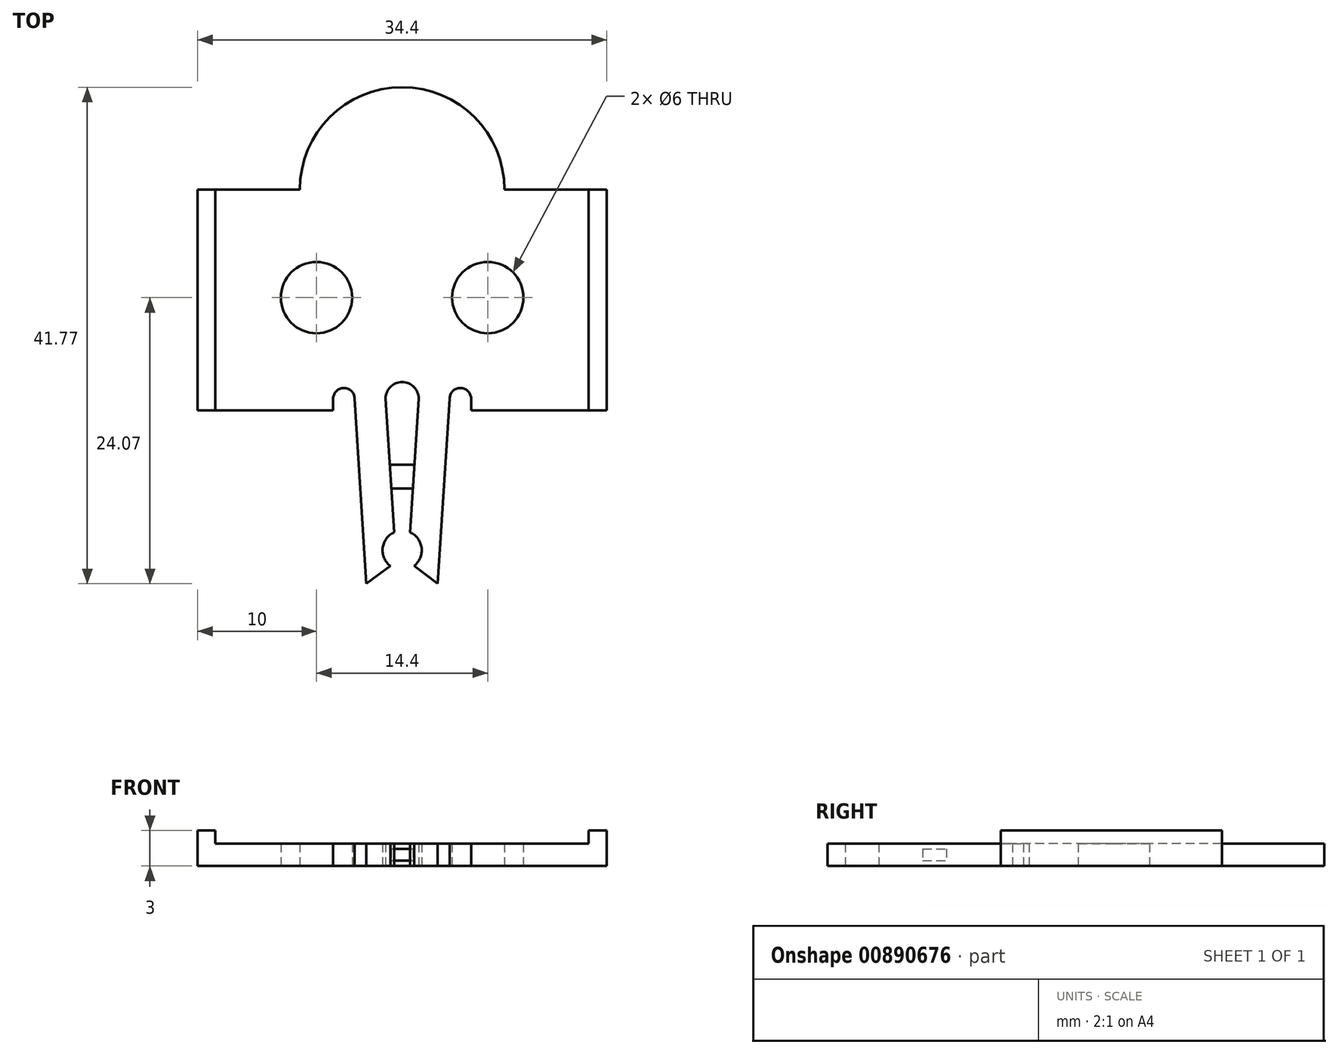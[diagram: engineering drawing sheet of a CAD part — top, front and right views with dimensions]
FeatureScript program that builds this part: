
annotation { "Feature Type Name" : "Feature", "Feature Type Description" : "" }
export const myFeature = defineFeature(function(context is Context, id is Id, definition is map)
    precondition{}
    {
        {
            var Q0;
            Q0=qCreatedBy(makeId("Top.planeOp"),FACE);
            var sketch = newSketch(context, id + "F0", { "sketchPlane" : qUnion([Q0])});
            skLineSegment(sketch, "E0", {"start": v(-5.8, 0) * mm, "end": v(-17.2, 0) * mm});
            skLineSegment(sketch, "E1", {"start": v(-17.2, 0) * mm, "end": v(-17.2, 18.6) * mm});
            skLineSegment(sketch, "E2", {"start": v(-17.2, 18.6) * mm, "end": v(0, 18.6) * mm});
            skLineSegment(sketch, "E3", {"start": v(-5.8, 0) * mm, "end": v(-5.8, 1) * mm});
            skLineSegment(sketch, "E4", {"start": v(-4, 1) * mm, "end": v(-3, -14.57) * mm});
            skLineSegment(sketch, "E5", {"start": v(-3, -14.57) * mm, "end": v(-1, -13.07) * mm});
            skLineSegment(sketch, "E6", {"start": v(-0.67, -10.25) * mm, "end": v(-0.67, -10.25) * mm});
            skLineSegment(sketch, "E7", {"start": v(-0.67, -10.25) * mm, "end": v(-1.4, 1) * mm});
            skArc(sketch, "E8", {"start": v(-1, -13.07) * mm, "mid": v(1.64, -11.95) * mm, "end": v(-0.67, -10.25) * mm, "construction": true});
            skArc(sketch, "E9", {"start": v(-0.67, -10.25) * mm, "mid": v(-1.64, -11.56) * mm, "end": v(-1, -13.07) * mm});
            skArc(sketch, "E10", {"start": v(-5.8, 1) * mm, "mid": v(-4.9, 0.1) * mm, "end": v(-4, 1) * mm, "construction": true});
            skArc(sketch, "E11", {"start": v(-4, 1) * mm, "mid": v(-4.9, 1.9) * mm, "end": v(-5.8, 1) * mm});
            skLineSegment(sketch, "E12", {"start": v(0, 0) * mm, "end": v(0, 3.93) * mm, "construction": true});
            skArc(sketch, "E13", {"start": v(-1.4, 1) * mm, "mid": v(0.99, 0.01) * mm, "end": v(0, 2.4) * mm, "construction": true});
            skArc(sketch, "E14", {"start": v(0, 2.4) * mm, "mid": v(-0.99, 1.99) * mm, "end": v(-1.4, 1) * mm});
            skArc(sketch, "E15.MirrorCS", {"start": v(1.4, 1) * mm, "mid": v(-0.99, 0.01) * mm, "end": v(0, 2.4) * mm, "construction": true});
            skCircle(sketch, "E16", {"center": v(-7.2, 9.5) * mm, "radius": 3 * mm});
            skLineSegment(sketch, "E17.MirrorCS", {"start": v(5.8, 0) * mm, "end": v(5.8, 1) * mm});
            skArc(sketch, "E18.MirrorCS", {"start": v(5.8, 1) * mm, "mid": v(4.9, 0.1) * mm, "end": v(4, 1) * mm, "construction": true});
            skArc(sketch, "E19.MirrorCS", {"start": v(0, 2.4) * mm, "mid": v(0.99, 1.99) * mm, "end": v(1.4, 1) * mm});
            skArc(sketch, "E20.MirrorCS", {"start": v(4, 1) * mm, "mid": v(4.9, 1.9) * mm, "end": v(5.8, 1) * mm});
            skArc(sketch, "E21.MirrorCS", {"start": v(0.67, -10.25) * mm, "mid": v(1.64, -11.56) * mm, "end": v(1, -13.07) * mm});
            skLineSegment(sketch, "E22.MirrorCS", {"start": v(3, -14.57) * mm, "end": v(1, -13.07) * mm});
            skArc(sketch, "E23.MirrorCS", {"start": v(1, -13.07) * mm, "mid": v(-1.64, -11.95) * mm, "end": v(0.67, -10.25) * mm, "construction": true});
            skLineSegment(sketch, "E24.MirrorCS", {"start": v(0.67, -10.25) * mm, "end": v(1.4, 1) * mm});
            skLineSegment(sketch, "E25.MirrorCS", {"start": v(4, 1) * mm, "end": v(3, -14.57) * mm});
            skCircle(sketch, "E26.MirrorC", {"center": v(7.2, 9.5) * mm, "radius": 3 * mm});
            skLineSegment(sketch, "E27.MirrorCS", {"start": v(5.8, 0) * mm, "end": v(17.2, 0) * mm});
            skLineSegment(sketch, "E28.MirrorCS", {"start": v(17.2, 18.6) * mm, "end": v(0, 18.6) * mm});
            skLineSegment(sketch, "E29.MirrorCS", {"start": v(17.2, 0) * mm, "end": v(17.2, 18.6) * mm});
            skLineSegment(sketch, "E30.MirrorCS", {"start": v(0.67, -10.25) * mm, "end": v(0.67, -10.25) * mm});
            skLineSegment(sketch, "E31", {"start": v(1.04, -4.57) * mm, "end": v(-1.04, -4.57) * mm});
            skLineSegment(sketch, "E32", {"start": v(-0.9, -6.57) * mm, "end": v(0.9, -6.57) * mm});
            skLineSegment(sketch, "E33", {"start": v(-15.7, 18.6) * mm, "end": v(-15.7, 0) * mm});
            skLineSegment(sketch, "E34", {"start": v(15.7, 18.6) * mm, "end": v(15.7, 0) * mm});
            skCircle(sketch, "E35", {"center": v(0, 18.6) * mm, "radius": 8.6 * mm});
            skSolve(sketch);
        }
        {
            var Q0;
            {var subQ11=sQuery(id+"F0.wireOp",EDGE,"E3");Q0=makeQuery(id+"F0.imprint","IMPRINT",FACE,{"disambiguationData":[TD([[makeQuery(id+"F0.imprint","IMPRINT",EDGE,{"derivedFrom":subQ11}),1.0]])]});}
            var Q1;
            {var subQ3=sQuery(id+"F0.wireOp",EDGE,"E28.MirrorCS");var subQ4=sQuery(id+"F0.wireOp",EDGE,"E2");var subQ5=makeQuery(id+"F0.imprint","INTERSECT",VERTEX,{"derivedFrom":[subQ4,subQ3]});Q1=makeQuery(id+"F0.imprint","IMPRINT",FACE,{"disambiguationData":[TD([[makeQuery(id+"F0.imprint","IMPRINT",EDGE,{"disambiguationData":[TD([[subQ5,1.0]])],"derivedFrom":subQ4}),-1.0]])]});}
            var Q2;
            {var subQ0=sQuery(id+"F0.wireOp",EDGE,"E28.MirrorCS");var subQ1=sQuery(id+"F0.wireOp",EDGE,"E2");var subQ2=makeQuery(id+"F0.imprint","INTERSECT",VERTEX,{"derivedFrom":[subQ1,subQ0]});Q2=makeQuery(id+"F0.imprint","IMPRINT",FACE,{"disambiguationData":[TD([[makeQuery(id+"F0.imprint","IMPRINT",EDGE,{"disambiguationData":[TD([[subQ2,1.0]])],"derivedFrom":subQ1}),1.0]])]});}
            extrude(context, id + "F1", {"entities" : qUnion([Q0, Q1, Q2]), "depth" : 1.9 * mm, "offsetDistance" : 25 * mm});
        }
        {
            var Q0;
            {var subQ0=sQuery(id+"F0.wireOp",EDGE,"E1");Q0=makeQuery(id+"F0.imprint","IMPRINT",FACE,{"disambiguationData":[TD([[makeQuery(id+"F0.imprint","IMPRINT",EDGE,{"derivedFrom":subQ0}),-1.0]])]});}
            var Q1;
            {var subQ0=sQuery(id+"F0.wireOp",EDGE,"E29.MirrorCS");Q1=makeQuery(id+"F0.imprint","IMPRINT",FACE,{"disambiguationData":[TD([[makeQuery(id+"F0.imprint","IMPRINT",EDGE,{"derivedFrom":subQ0}),1.0]])]});}
            extrude(context, id + "F2", {"entities" : qUnion([Q0, Q1]), "operationType" : NewBodyOperationType.ADD, "depth" : 3 * mm, "offsetDistance" : 25 * mm});
        }
        {
            var Q0;
            {var subQ0=sQuery(id+"F0.wireOp",EDGE,"E31");Q0=makeQuery(id+"F0.imprint","IMPRINT",FACE,{"disambiguationData":[TD([[makeQuery(id+"F0.imprint","IMPRINT",EDGE,{"derivedFrom":subQ0}),1.0]])]});}
            extrude(context, id + "F3", {"entities" : qUnion([Q0]), "operationType" : NewBodyOperationType.ADD, "depth" : (1 + 0.9 / 2) * mm, "offsetDistance" : 25 * mm});
        }
        {
            var Q0;
            {var subQ0=sQuery(id+"F0.wireOp",EDGE,"E31");Q0=makeQuery(id+"F0.imprint","IMPRINT",FACE,{"disambiguationData":[TD([[makeQuery(id+"F0.imprint","IMPRINT",EDGE,{"derivedFrom":subQ0}),1.0]])]});}
            extrude(context, id + "F4", {"entities" : qUnion([Q0]), "operationType" : NewBodyOperationType.REMOVE, "depth" : (0.9 / 2) * mm, "offsetDistance" : 25 * mm});
        }
    });
